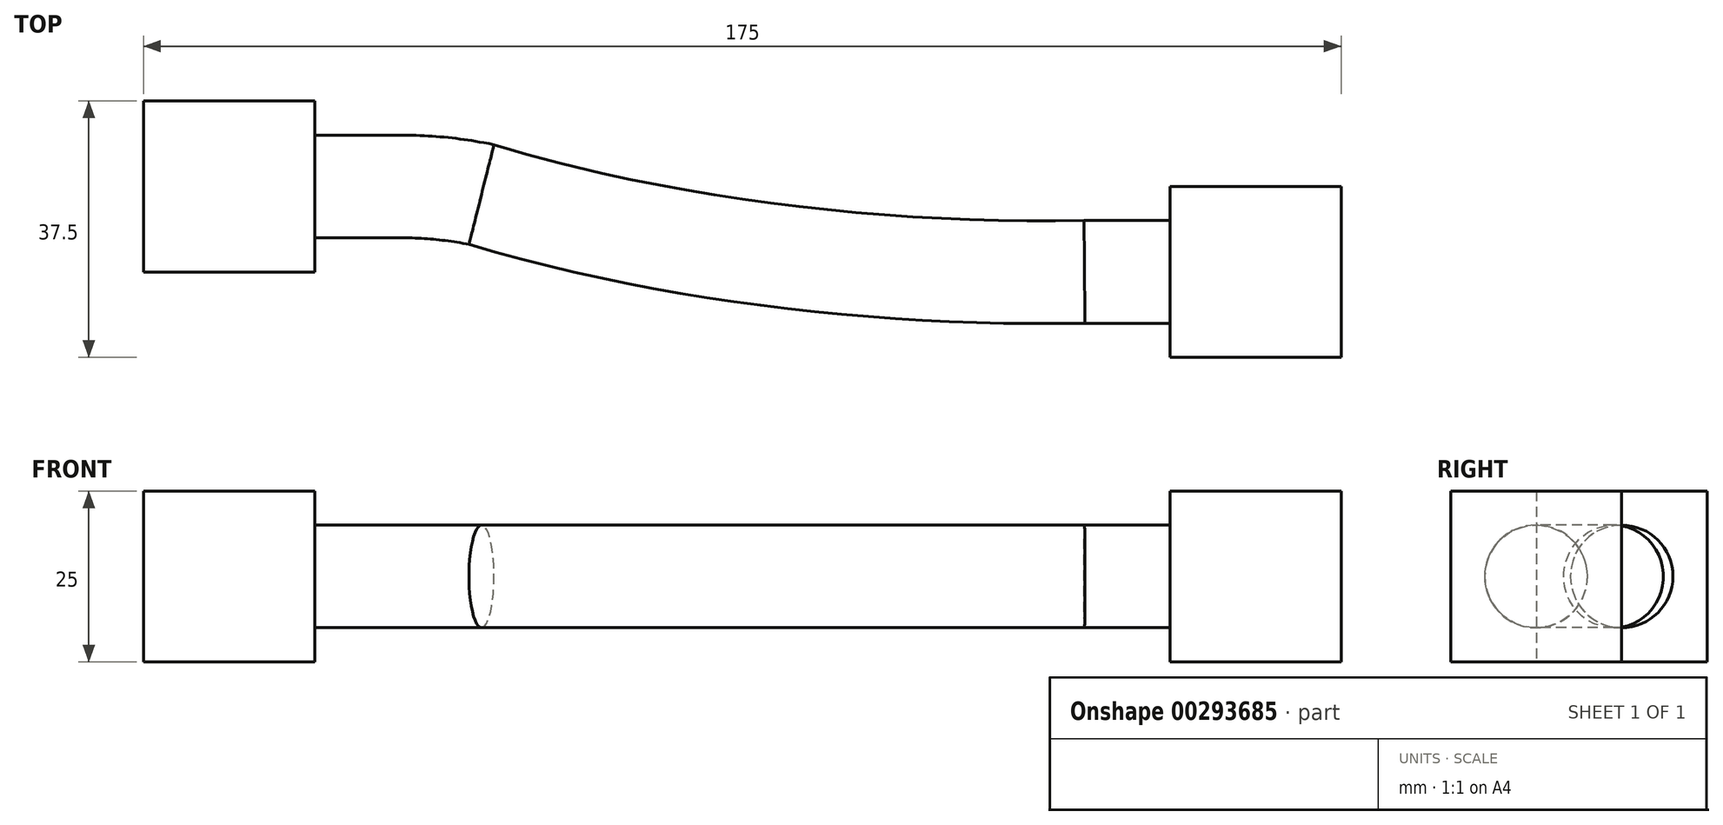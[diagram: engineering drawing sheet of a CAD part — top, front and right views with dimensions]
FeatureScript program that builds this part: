
annotation { "Feature Type Name" : "Feature", "Feature Type Description" : "" }
export const myFeature = defineFeature(function(context is Context, id is Id, definition is map)
    precondition{}
    {
        {
            var Q0;
            Q0=qCreatedBy(makeId("Top.planeOp"),FACE);
            var sketch = newSketch(context, id + "F0", { "sketchPlane" : qUnion([Q0])});
            skLineSegment(sketch, "E0.bottom", {"start": v(-137.5, 25) * mm, "end": v(-112.5, 25) * mm});
            skLineSegment(sketch, "E0.top", {"start": v(-137.5, 0) * mm, "end": v(-112.5, 0) * mm});
            skLineSegment(sketch, "E0.left", {"start": v(-137.5, 25) * mm, "end": v(-137.5, 0) * mm});
            skLineSegment(sketch, "E0.right", {"start": v(-112.5, 25) * mm, "end": v(-112.5, 0) * mm});
            skLineSegment(sketch, "E1.bottom", {"start": v(12.5, 12.5) * mm, "end": v(37.5, 12.5) * mm});
            skLineSegment(sketch, "E1.top", {"start": v(12.5, -12.5) * mm, "end": v(37.5, -12.5) * mm});
            skLineSegment(sketch, "E1.left", {"start": v(12.5, 12.5) * mm, "end": v(12.5, -12.5) * mm});
            skLineSegment(sketch, "E1.right", {"start": v(37.5, 12.5) * mm, "end": v(37.5, -12.5) * mm});
            skLineSegment(sketch, "E2", {"start": v(-112.5, 12.5) * mm, "end": v(-100, 12.5) * mm});
            skLineSegment(sketch, "E3", {"start": v(0, 0) * mm, "end": v(12.5, 0) * mm});
            skLineSegment(sketch, "E4", {"start": v(-112.5, 12.5) * mm, "end": v(-137.5, 12.5) * mm, "construction": true});
            skLineSegment(sketch, "E5", {"start": v(-125, 12.5) * mm, "end": v(-125, 28.35) * mm, "construction": true});
            skPoint(sketch, "E5.endSnap0", {"position": v(-125, 25) * mm});
            skLineSegment(sketch, "E6", {"start": v(25, -12.5) * mm, "end": v(25, -19.18) * mm, "construction": true});
            skArc(sketch, "E7", {"start": v(-88.11, 11.31) * mm, "mid": v(-94.03, 12.2) * mm, "end": v(-100, 12.5) * mm});
            skLineSegment(sketch, "E8", {"start": v(25, 12.5) * mm, "end": v(25, 0) * mm, "construction": true});
            skLineSegment(sketch, "E9", {"start": v(12.5, 0) * mm, "end": v(37.5, 0) * mm, "construction": true});
            skFitSpline(sketch, "E10", {"points": [v(0, 0) * mm, v(-88.11, 11.31) * mm], "startDerivative": vector(-86.94, -1.58) * mm, "endDerivative": vector(-81.86, 24.83) * mm});
            skSolve(sketch);
        }
        {
            var Q0;
            {var subQ1=sQuery(id+"F0.wireOp",EDGE,"E0.bottom");Q0=makeQuery(id+"F0.imprint","IMPRINT",FACE,{"disambiguationData":[TD([[makeQuery(id+"F0.imprint","IMPRINT",EDGE,{"derivedFrom":subQ1}),-1.0]])]});}
            var Q1;
            {var subQ3=sQuery(id+"F0.wireOp",EDGE,"E1.bottom");Q1=makeQuery(id+"F0.imprint","IMPRINT",FACE,{"disambiguationData":[TD([[makeQuery(id+"F0.imprint","IMPRINT",EDGE,{"derivedFrom":subQ3}),-1.0]])]});}
            extrude(context, id + "F1", {"entities" : qUnion([Q0, Q1]), "endBound" : BoundingType.SYMMETRIC, "depth" : 25 * mm});
        }
        {
            var Q0;
            Q0=makeQuery(id+"F1.opExtrude","SWEPT_FACE",FACE,{"disambiguationData":[OSD([sQuery(id+"F0.wireOp",EDGE,"E0.right")])]});
            var sketch = newSketch(context, id + "F2", { "sketchPlane" : qUnion([Q0])});
            skCircle(sketch, "E11", {"center": v(12.5, 0) * mm, "radius": 7.5 * mm});
            skSolve(sketch);
        }
        {
            var Q0;
            Q0=makeQuery(id+"F2.imprint","IMPRINT",FACE,{"disambiguationData":[TD([[makeQuery(id+"F2.imprint","IMPRINT",EDGE,{"derivedFrom":sQuery(id+"F2.wireOp",EDGE,"E11")}),1.0]])]});
            var Q1;
            Q1=sQuery(id+"F0.wireOp",EDGE,"E2");
            var Q2;
            Q2=sQuery(id+"F0.wireOp",EDGE,"E7");
            var Q3;
            Q3=sQuery(id+"F0.wireOp",EDGE,"E10");
            var Q4;
            Q4=sQuery(id+"F0.wireOp",EDGE,"E3");
            sweep(context, id + "F3", {"profiles" : qUnion([Q0]), "path" : qUnion([Q1, Q2, Q3, Q4])});
        }
    });
